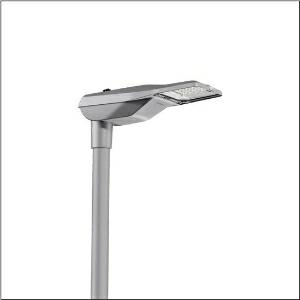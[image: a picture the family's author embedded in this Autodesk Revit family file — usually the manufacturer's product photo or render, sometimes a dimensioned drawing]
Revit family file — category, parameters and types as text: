
# Revit family: streetlight_sl_21_iq_micro___p0_5a_5xe1v31v08cb_beee
name_source: partatom
category: Lighting Fixtures
units: mm (PartAtom-declared; Revit-internal decimal feet)

## family parameters
Cut with Voids When Loaded = No
Host = Face
Light Source = No
Part Type = Normal
Room Calculation Point = No
Round Connector Dimension = Use Diameter
Shared = No

## types (1)
- --- (1 x LED, 2840 lm, 19.1 W, 3000K)
    Apparent Load = 19 VA
    CIE Flux Codes = 37 73 96 100 100
    Color Rendering = 70
    Color Temperature = 3000K
    Default Elevation = 1800 mm
    Description = Streetlight SL 21 iQ micro, mast luminaire, primary light control with lens, of PMMA, primary optical cover: cover, of toughened safety glass, transparent, light distribution: P0.5a, light emission: direct distribution, primary light characteristic: asymmetric, installation type: post-top, side-entry, LED, High Power LED, rated luminous flux: 2.840lm, luminous efficacy: 149lm/W, light colour: 730, colour temperature: 3000K, control gear: iQ-Street Remote, D4i with power reduction, control: pre-setting: logarithmic dimming characteristic, Street-Remote, Auto-Match, Temp-Guard, Lumen-Switch, Night-Set, Smart-Wire, Light-Fading, Desk-Remote (wireless, voltage-free reading and setting of iQ features in the workshop via application-optimized NFC function/RFID function), optimised constant luminous flux control (CLO 2.0), mains connection: 220..240V, AC, 50/60Hz, start of lifetime: 19W, end of service life: 20W, reduction: 9W, luminaire housing, of diecast aluminium, powder-coated, Siteco® metallic grey (DB 702S), corrosivity category C5 mid according to DIN EN ISO 12944, please order mast flange separately, inclination adjustable: 0°, 5°, 10°, 15°, sealing non-destructively replaceable, multi-level sealing system, length: 528mm, width: 235mm, height: 110mm, mast flange for spigot size: 42mm (side-entry): 5XC10008XM4, 60/48mm (side-entry/post-top): 5XC10108XM2, 76/60mm (side-entry/post-top): 5XC10108XM1, mounting height: 4..8m, Smart Interface above, protection rating (complete): IP66, insulation class (complete): insulation class II (safety insulation), certification: CE, ENEC, ENEC+, VDE, impact resistance: IK10, permissible operating ambient temperature for outdoor applications: -40..+50°C, standard-compliant lighting for roads and squares, packaging unit: 1 piece

Light Distribution: P0.5a
    Height = 110 mm
    Lamp = 1 x LED
    Lamp Light Flux = 2840 lm
    Lamp Power = 19.1 W
    Lamp count = 1
    Length = 528 mm
    Luminous efficacy = 149 lm/W
    Manufacturer = Siteco
    ModVariant = No
    Model = 5XE1V31V08CB
    Number of Poles = 1
    OnlyDefault = Yes
    Power Factor = 1
    Product Name = Streetlight SL 21 iQ micro | P0.5a
    Product group = mast luminaire | pylon top
    ProductGroupID = 6100
    Protection Class = Protection class II
    Protection Degree = IP 66
    RLX_Detail_Level = 1
    RLX_Emergency_Light_Flux = 0 lm
    RLX_Emergency_Type = 0
    RLX_Emergency_Type_DB = No
    RlxData = <blob elided: 97861 chars, md5=35a1c4e0>
    Socket = socket
    Standby Power = 0 W
    System Light Flux = 2840 lm
    System Power = 19 W
    Type Comments = factory setting: luminous flux: 100 % | dim-lin: 254 | 387 mA
    Type Image = l_1277292.jpg
    URL = http://relux.com
    VarID = @adj_070218
    Voltage = 0 V
    Weight = 0.00 kg
    Width = 235 mm

## geometry (parser evidence)
native form markers: Blend x4, Sweep x11
no freeform markers — native parametric forms only
